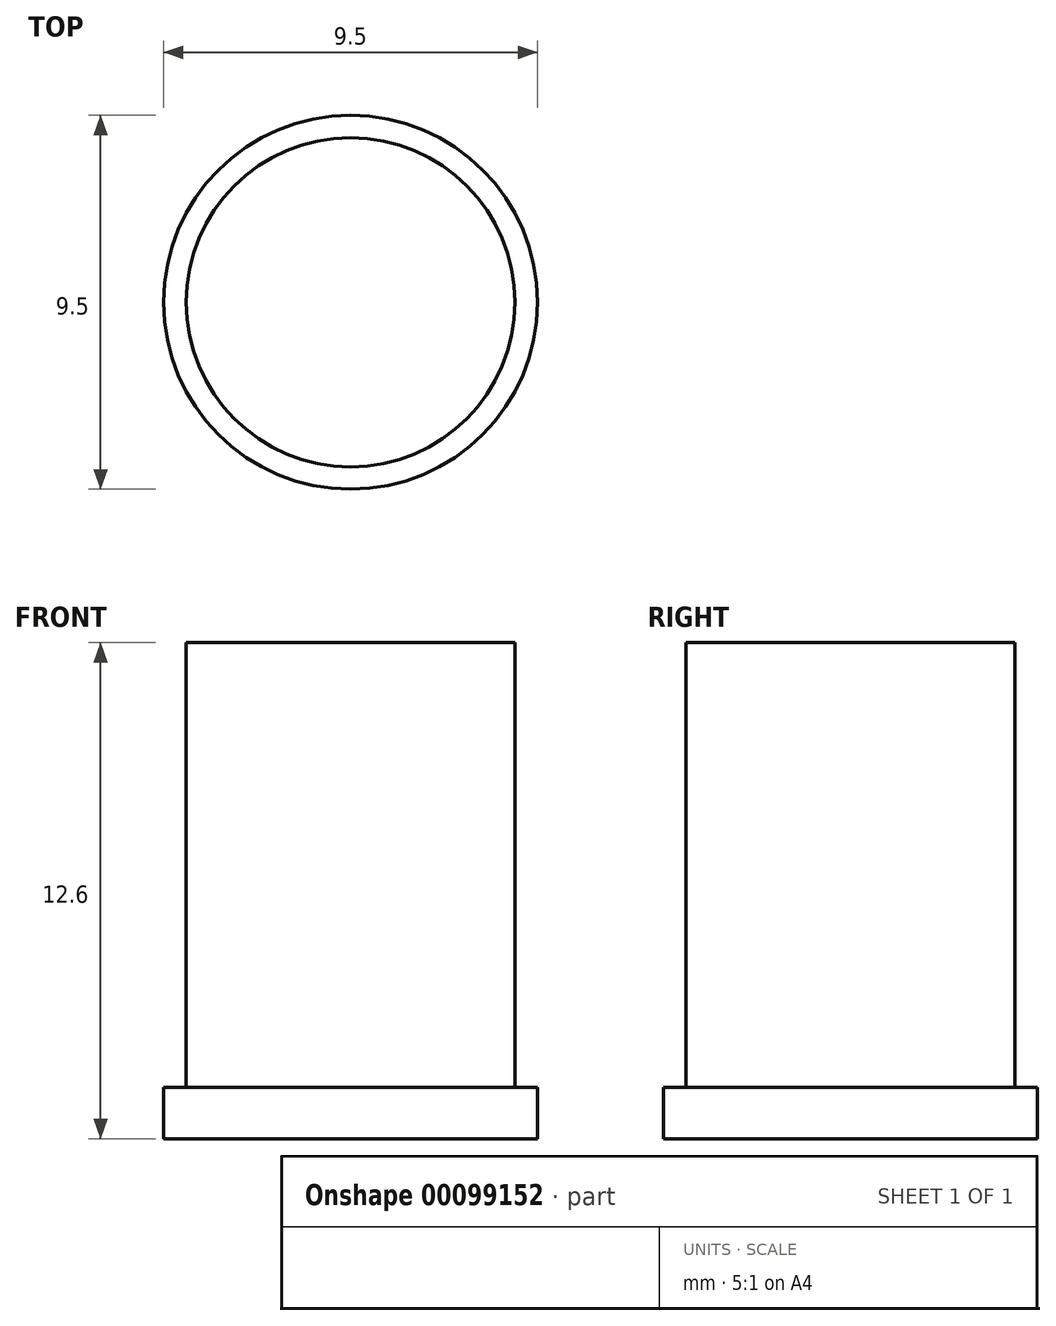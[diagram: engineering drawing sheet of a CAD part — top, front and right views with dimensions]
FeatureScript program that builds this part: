
annotation { "Feature Type Name" : "Feature", "Feature Type Description" : "" }
export const myFeature = defineFeature(function(context is Context, id is Id, definition is map)
    precondition{}
    {
        {
            var Q0;
            Q0=qCreatedBy(makeId("Front.planeOp"),FACE);
            var sketch = newSketch(context, id + "F0", { "sketchPlane" : qUnion([Q0])});
            skLineSegment(sketch, "E0", {"start": v(0, 12.6) * mm, "end": v(0, 0) * mm});
            skLineSegment(sketch, "E1", {"start": v(0, 0) * mm, "end": v(4.75, 0) * mm});
            skLineSegment(sketch, "E2", {"start": v(4.75, 0) * mm, "end": v(4.75, 1.3) * mm});
            skLineSegment(sketch, "E3", {"start": v(4.75, 1.3) * mm, "end": v(4.18, 1.3) * mm});
            skLineSegment(sketch, "E4", {"start": v(4.18, 1.3) * mm, "end": v(4.18, 12.6) * mm});
            skLineSegment(sketch, "E5", {"start": v(4.18, 12.6) * mm, "end": v(0, 12.6) * mm});
            skSolve(sketch);
        }
        {
            var Q0;
            Q0 = qSketchRegion(id + "F0", true);
            var Q1;
            Q1=sQuery(id+"F0.wireOp",EDGE,"E0");
            revolve(context, id + "F1", {"entities" : qUnion([Q0]), "axis" : qUnion([Q1]), "revolveType" : RevolveType.FULL});
        }
    });
